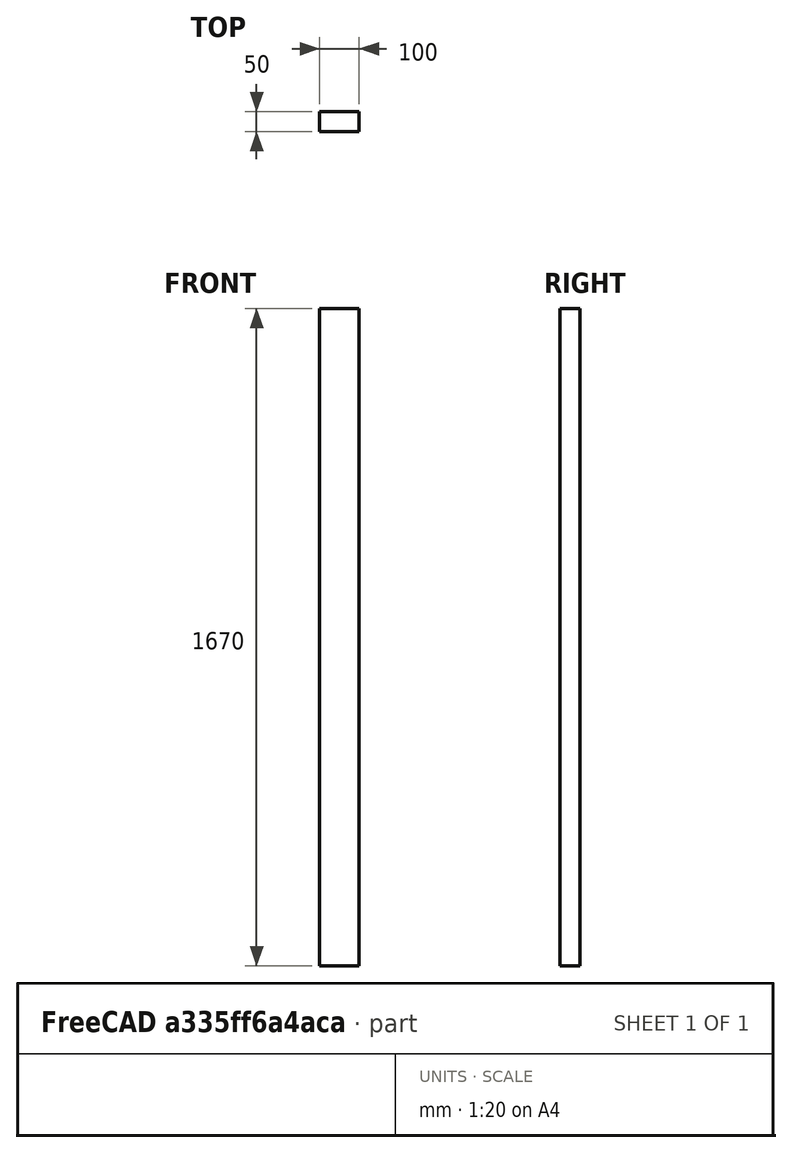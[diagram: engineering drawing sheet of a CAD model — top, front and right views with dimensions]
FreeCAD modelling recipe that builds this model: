
FCSTD DOCUMENT  (FreeCAD 1.0R39109 (Git))
Label: 046_table_bottom_frame_large
License: All rights reserved
LicenseURL: http://en.wikipedia.org/wiki/All_rights_reserved
objects: Sketcher::SketchObject×1, Spreadsheet::Sheet×1, PartDesign::Pad×1, PartDesign::Body×1
note: 6 computed .brp shape members not serialized (recipe doc carries the construction recipe); baked Part::Feature solids carry a one-line shape summary decoded from their .brp

FEATURE [Sketcher::SketchObject] Sketch
  ArcFitTolerance = 1e-06
  AttachmentSupport = -> [XY_Plane]
  FullyConstrained = true
  MakeInternals = false
  MapMode = 5
  expr: Constraints[11] = Spreadsheet.width
  expr: Constraints[12] = Spreadsheet.length
  sketch-geometry (5):
    g0: LineSegment StartX=-50 StartY=25 StartZ=0 EndX=-50 EndY=-25 EndZ=0
    g1: LineSegment StartX=-50 StartY=-25 StartZ=0 EndX=50 EndY=-25 EndZ=0
    g2: LineSegment StartX=50 StartY=-25 StartZ=0 EndX=50 EndY=25 EndZ=0
    g3: LineSegment StartX=50 StartY=25 StartZ=0 EndX=-50 EndY=25 EndZ=0
    g4: LineSegment [constr] StartX=-50 StartY=25 StartZ=0 EndX=50 EndY=-25 EndZ=0
  constraints (13):
    c: Coincident(g0,g1)
    c: Coincident(g1,g2)
    c: Coincident(g2,g3)
    c: Coincident(g3,g0)
    c: Vertical(g0)
    c: Vertical(g2)
    c: Horizontal(g1)
    c: Horizontal(g3)
    c: Coincident(g4,g0)
    c: Coincident(g4,g1)
    c: Symmetric(g4,g4,g-1)
    c: Distance(g0,g0) = 50
    c: Distance(g3,g3) = 100
FEATURE [Spreadsheet::Sheet] Spreadsheet
  cells = A2='length; B2(length)=100; A3='width; B3(width)=50; A4='height; B4(height)=1670
FEATURE [PartDesign::Pad] Pad
  Direction = (0,0,1)
  Length = 1670
  Length2 = 10
  Midplane = true
  Profile = -> Sketch
  ReferenceAxis = -> Sketch [N_Axis]
  Suppressed = false
  Type = 0
  expr: Length = Spreadsheet.height
FEATURE [PartDesign::Body] Body
  AllowCompound = false
  Group = -> [Sketch,Pad]
  Origin = -> Origin
  Tip = -> Pad
